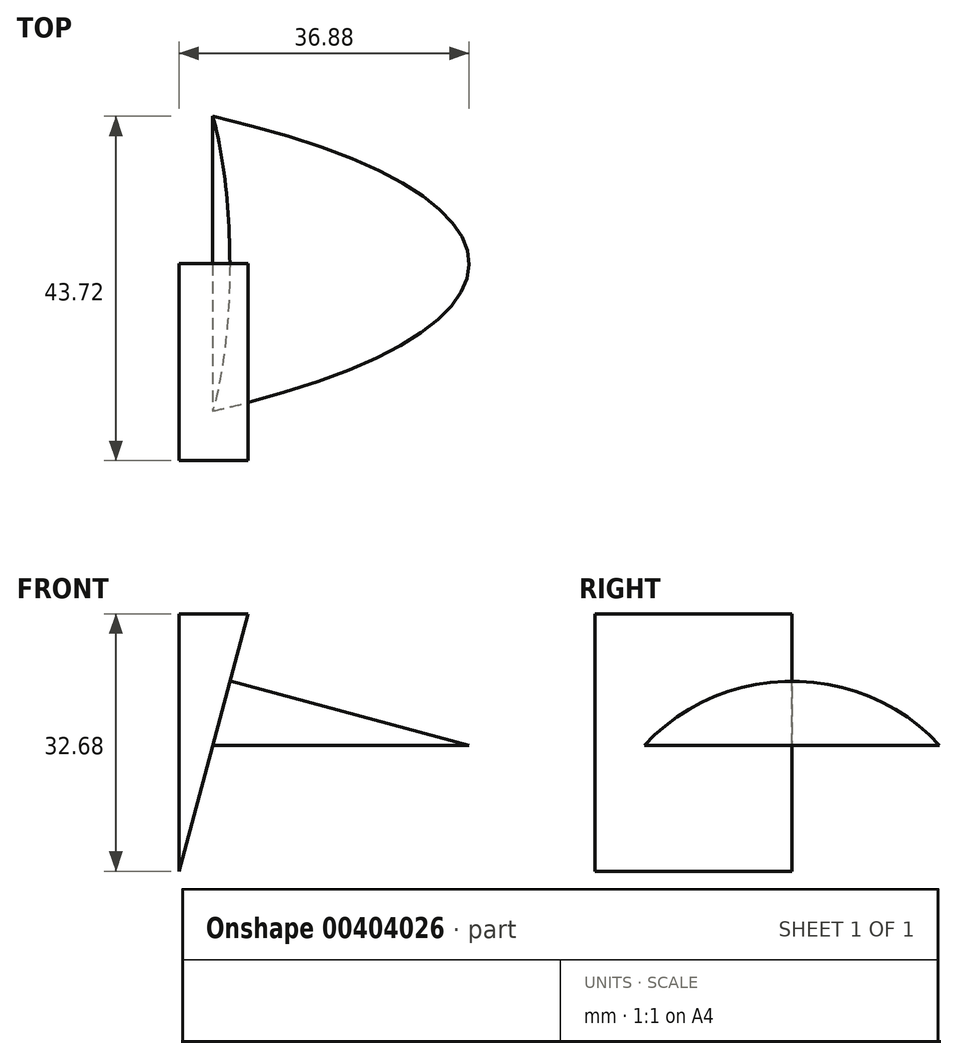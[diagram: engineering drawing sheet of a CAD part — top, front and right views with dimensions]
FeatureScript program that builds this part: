
annotation { "Feature Type Name" : "Feature", "Feature Type Description" : "" }
export const myFeature = defineFeature(function(context is Context, id is Id, definition is map)
    precondition{}
    {
        {
            var Q0;
            Q0=qCreatedBy(makeId("Front.planeOp"),FACE);
            var sketch = newSketch(context, id + "F0", { "sketchPlane" : qUnion([Q0])});
            skLineSegment(sketch, "E0", {"start": v(0, 0) * mm, "end": v(8.76, 32.68) * mm});
            skLineSegment(sketch, "E1", {"start": v(8.76, 32.68) * mm, "end": v(0, 32.68) * mm});
            skLineSegment(sketch, "E2", {"start": v(0, 32.68) * mm, "end": v(0, 0) * mm});
            skSolve(sketch);
        }
        {
            var Q0;
            Q0 = qSketchRegion(id + "F0", true);
            extrude(context, id + "F1", {"entities" : qUnion([Q0]), "depth" : 25 * mm});
        }
        {
            var Q0;
            Q0=makeQuery(id+"F1.opExtrude","SWEPT_FACE",FACE,{"disambiguationData":[OSD([sQuery(id+"F0.wireOp",EDGE,"E0")])]});
            cPlane(context, id + "F2", {"entities" : qUnion([Q0]), "cplaneType" : CPlaneType.OFFSET, "offset" : 0 * mm, "width" : 150 * mm, "height" : 150 * mm});
        }
        {
            var Q0;
            Q0=qCreatedBy(id+"F2.planeOp",FACE);
            var sketch = newSketch(context, id + "F3", { "sketchPlane" : qUnion([Q0])});
            skCircle(sketch, "E3", {"center": v(0, 0) * mm, "radius": 25 * mm});
            skSolve(sketch);
        }
        {
            var Q0;
            Q0 = qSketchRegion(id + "F3", true);
            extrude(context, id + "F4", {"entities" : qUnion([Q0]), "depth" : 50 * mm});
        }
        {
            var Q0;
            Q0=qCreatedBy(makeId("Front.planeOp"),FACE);
            var sketch = newSketch(context, id + "F5", { "sketchPlane" : qUnion([Q0])});
            skLineSegment(sketch, "E4.bottom", {"start": v(-25, 16) * mm, "end": v(65, 16) * mm});
            skLineSegment(sketch, "E4.top", {"start": v(-25, -74) * mm, "end": v(65, -74) * mm});
            skLineSegment(sketch, "E4.left", {"start": v(-25, 16) * mm, "end": v(-25, -74) * mm});
            skLineSegment(sketch, "E4.right", {"start": v(65, 16) * mm, "end": v(65, -74) * mm});
            skSolve(sketch);
        }
        {
            var Q0;
            Q0 = qSketchRegion(id + "F5", true);
            extrude(context, id + "F6", {"entities" : qUnion([Q0]), "endBound" : BoundingType.SYMMETRIC, "depth" : 75 * mm});
        }
        {
            var Q0;
            Q0=makeQuery(id+"F6.opExtrude","SWEPT_BODY",BODY,{"disambiguationData":[OSD([sQuery(id+"F5.wireOp",EDGE,"E4.bottom"),sQuery(id+"F5.wireOp",EDGE,"E4.top"),sQuery(id+"F5.wireOp",EDGE,"E4.left"),sQuery(id+"F5.wireOp",EDGE,"E4.right")])]});
            var Q1;
            Q1=makeQuery(id+"F4.opExtrude","SWEPT_BODY",BODY,{"disambiguationData":[OSD([sQuery(id+"F3.wireOp",EDGE,"E3")])]});
            booleanBodies(context, id + "F7", {"operationType" : BooleanOperationType.SUBTRACTION, "tools" : qUnion([Q0]), "targets" : qUnion([Q1])});
        }
    });
